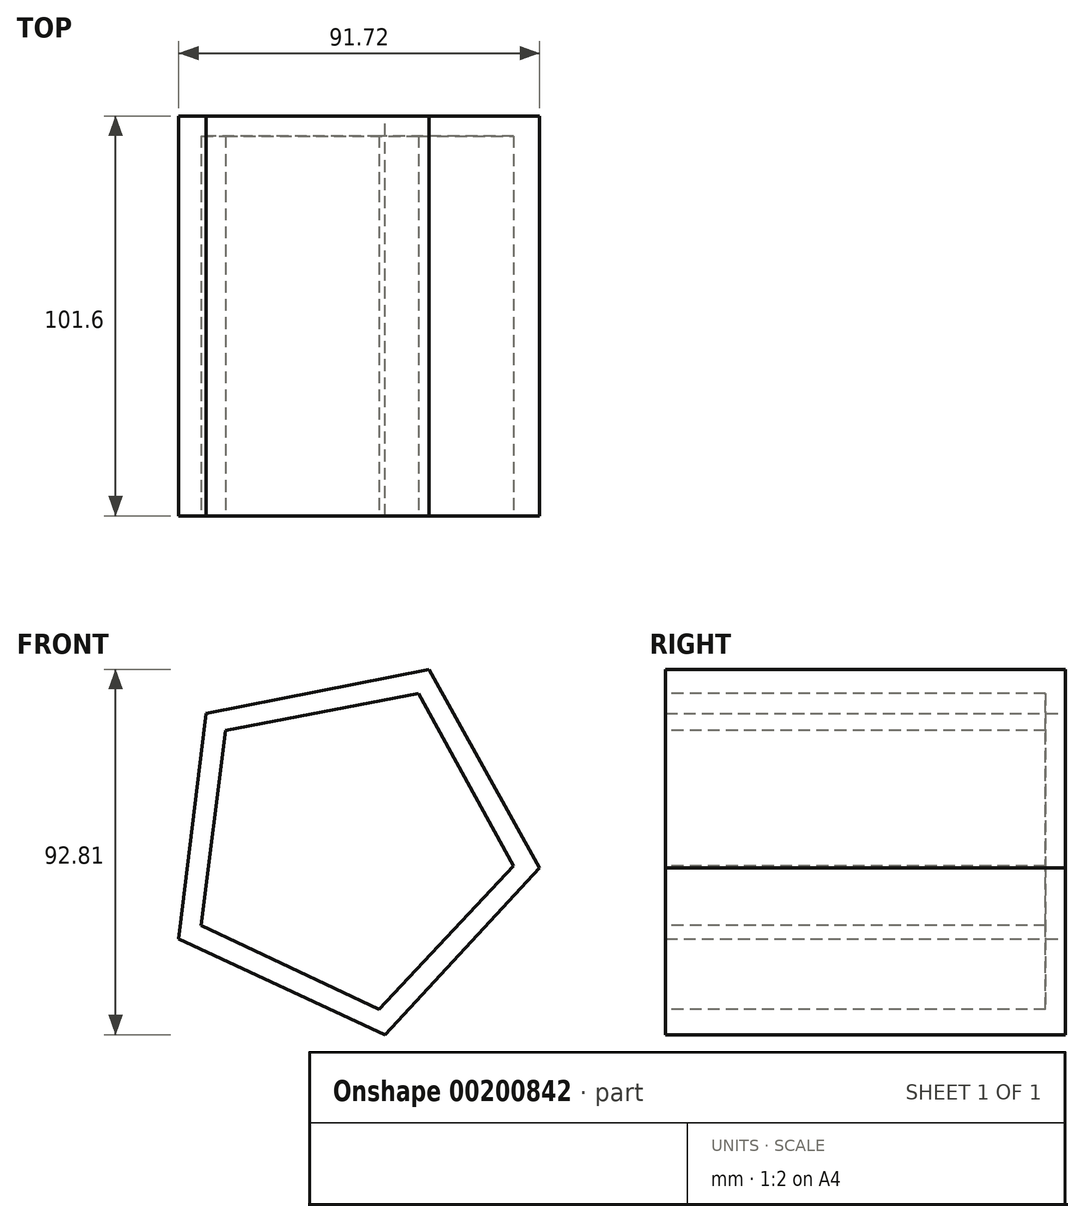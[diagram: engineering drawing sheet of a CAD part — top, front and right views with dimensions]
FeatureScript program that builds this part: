
annotation { "Feature Type Name" : "Feature", "Feature Type Description" : "" }
export const myFeature = defineFeature(function(context is Context, id is Id, definition is map)
    precondition{}
    {
        {
            var Q0;
            Q0=qCreatedBy(makeId("Front.planeOp"),FACE);
            var sketch = newSketch(context, id + "F0", { "sketchPlane" : qUnion([Q0])});
            skCircle(sketch, "E0.cCircle", {"center": v(0, 0) * mm, "radius": 39.76 * mm, "construction": true});
            skLineSegment(sketch, "E0.0", {"start": v(20.67, 44.59) * mm, "end": v(48.8, -5.88) * mm});
            skLineSegment(sketch, "E0.1", {"start": v(48.8, -5.88) * mm, "end": v(9.49, -48.22) * mm});
            skLineSegment(sketch, "E0.2", {"start": v(9.49, -48.22) * mm, "end": v(-42.93, -23.92) * mm});
            skLineSegment(sketch, "E0.3", {"start": v(-42.93, -23.92) * mm, "end": v(-36.02, 33.43) * mm});
            skLineSegment(sketch, "E0.4", {"start": v(-36.02, 33.43) * mm, "end": v(20.67, 44.59) * mm});
            skPoint(sketch, "E0.0.midPoint", {"position": v(34.73, 19.35) * mm});
            skSolve(sketch);
        }
        {
            var Q0;
            Q0 = qSketchRegion(id + "F0", true);
            extrude(context, id + "F1", {"entities" : qUnion([Q0]), "depth" : 101.6 * mm});
        }
        {
            var Q0;
            Q0=makeQuery(id+"F1.opExtrude","CAP_FACE",FACE,{"disambiguationData":[OSD([sQuery(id+"F0.wireOp",EDGE,"E0.0"),sQuery(id+"F0.wireOp",EDGE,"E0.1"),sQuery(id+"F0.wireOp",EDGE,"E0.2"),sQuery(id+"F0.wireOp",EDGE,"E0.3"),sQuery(id+"F0.wireOp",EDGE,"E0.4")])],"isStart":false});
            var sketch = newSketch(context, id + "F2", { "sketchPlane" : qUnion([Q0])});
            skCircle(sketch, "E1.cCircle", {"center": v(0, 0) * mm, "radius": 34.4 * mm, "construction": true});
            skLineSegment(sketch, "E1.0", {"start": v(18.07, 38.48) * mm, "end": v(42.18, -5.3) * mm});
            skLineSegment(sketch, "E1.1", {"start": v(42.18, -5.3) * mm, "end": v(8, -41.75) * mm});
            skLineSegment(sketch, "E1.2", {"start": v(8, -41.75) * mm, "end": v(-37.23, -20.51) * mm});
            skLineSegment(sketch, "E1.3", {"start": v(-37.23, -20.51) * mm, "end": v(-31.01, 29.07) * mm});
            skLineSegment(sketch, "E1.4", {"start": v(-31.01, 29.07) * mm, "end": v(18.07, 38.48) * mm});
            skPoint(sketch, "E1.0.midPoint", {"position": v(30.12, 16.6) * mm});
            skSolve(sketch);
        }
        {
            var Q0;
            Q0 = qSketchRegion(id + "F2", true);
            extrude(context, id + "F3", {"entities" : qUnion([Q0]), "operationType" : NewBodyOperationType.REMOVE, "oppositeDirection" : true, "depth" : 96.52 * mm});
        }
    });
